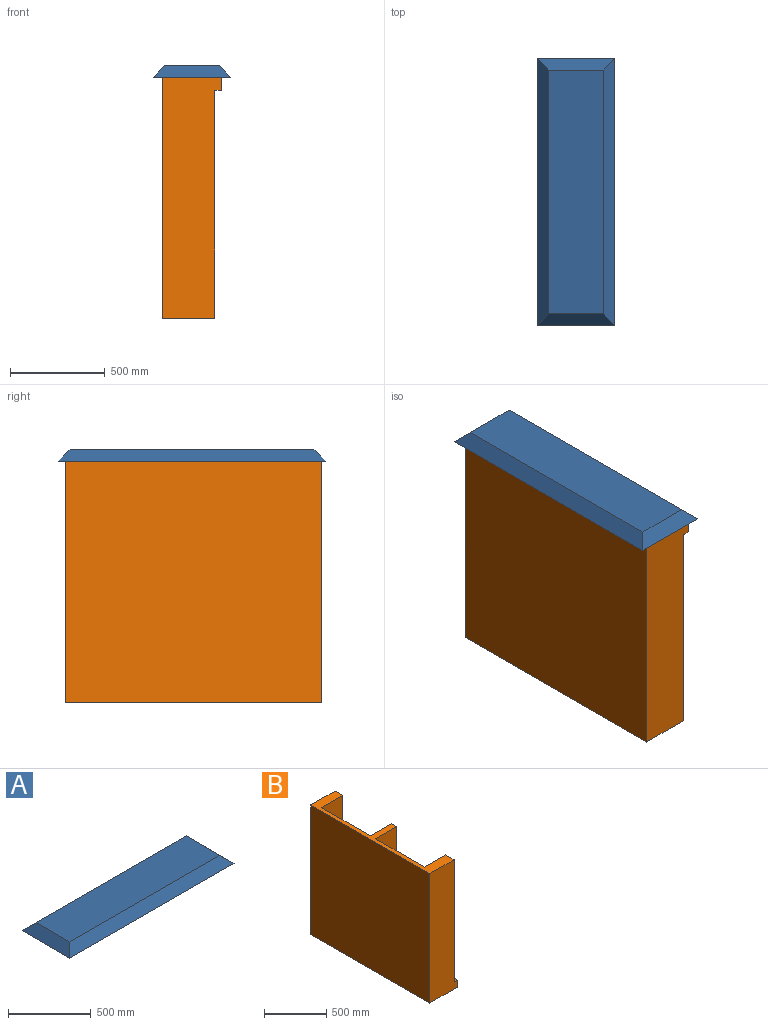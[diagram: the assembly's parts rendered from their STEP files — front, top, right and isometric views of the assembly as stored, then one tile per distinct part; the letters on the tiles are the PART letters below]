
ASSEMBLY  parts=2 mates=1
PART A: 6 faces, bbox 1405x410x60 mm
  f0: plane 1285x290mm, normal (0,0,1), area 372650mm2, adj f2,f3,f4,f5
  f1: plane 1405x410mm, normal (0,0,-1), area 576050mm2, adj f2,f3,f4,f5
  f2: plane 1405x60mm, normal (0,0.71,0.71), area 114127mm2, adj f0,f1,f3,f4
  f3: plane 410x60mm, normal (0.71,0,0.71), area 29698.5mm2, adj f0,f1,f2,f5
  f4: plane 410x60mm, normal (-0.71,0,0.71), area 29698.5mm2, adj f0,f1,f2,f5
  f5: plane 1405x60mm, normal (0,-0.71,0.71), area 114127mm2, adj f0,f1,f3,f4
PART B: 34 faces, bbox 310x1350x1270 mm
  f0: plane 345x240mm, normal (0,1,0), area 82800mm2, adj f2,f23,f28,f33
  f1: plane 285x240mm, normal (0,1,0), area 68400mm2, adj f13,f23,f26,f32
  f2: plane 554.25x345mm, normal (1,0,0), area 191217.5mm2, adj f0,f10,f28,f33
  f3: plane 553x345mm, normal (1,0,0), area 190785mm2, adj f4,f11,f27,f30
  f4: plane 345x240mm, normal (0,-1,0), area 82800mm2, adj f3,f23,f27,f30
  f5: plane 285x240mm, normal (0,-1,0), area 68400mm2, adj f13,f23,f26,f32
  f6: plane 285x240mm, normal (0,1,0), area 68400mm2, adj f16,f23,f26,f31
  f7: plane 240x70mm, normal (0,1,0), area 16800mm2, adj f8,f12,f15,f21
  f8: plane 1167.25x520mm, normal (1,0,0), area 602771.9mm2, adj f7,f9,f12,f21,f24,f25,f29
  f9: plane 520x240mm, normal (0,-1,0), area 124800mm2, adj f8,f15,f21,f23,f29
  f10: plane 345x240mm, normal (0,-1,0), area 82800mm2, adj f2,f23,f28,f33
  f11: plane 345x240mm, normal (0,1,0), area 82800mm2, adj f3,f23,f27,f30
  f12: plane 1350x275mm, normal (0,0,1), area 61650mm2, adj f7,f8,f14,f15,f18,f19,f20,f23
  f13: plane 554.25x285mm, normal (1,0,0), area 157962.3mm2, adj f1,f5,f26,f32
  f14: plane 554.25x70mm, normal (-1,0,0), area 38797.8mm2, adj f12,f21,f24,f25
  f15: plane 553x70mm, normal (-1,0,0), area 38710mm2, adj f7,f9,f12,f21
  f16: plane 553x285mm, normal (1,0,0), area 157605mm2, adj f6,f22,f26,f31
  f17: plane 1350x1270mm, normal (-1,0,0), area 1714500mm2, adj f18,f20,f21,f26
  f18: plane 1270x310mm, normal (0,-1,0), area 351700mm2, adj f12,f17,f19,f21,f23,f26
  f19: plane 1350x70mm, normal (1,0,0), area 94500mm2, adj f12,f18,f20,f21
  f20: plane 1270x310mm, normal (0,1,0), area 351700mm2, adj f12,f17,f19,f21,f23,f26
  f21: plane 1350x310mm, normal (0,0,-1), area 152759.1mm2, adj f7,f8,f9,f14,f15,f17,f18,f19
  f22: plane 285x240mm, normal (0,-1,0), area 68400mm2, adj f16,f23,f26,f31
  f23: plane 1350x1200mm, normal (1,0,0), area 397166.1mm2, adj f0,f1,f4,f5,f6,f9,f10,f11
  f24: plane 520x240mm, normal (0,1,0), area 124800mm2, adj f8,f14,f21,f23,f29
  f25: plane 240x70mm, normal (0,-1,0), area 16800mm2, adj f8,f12,f14,f21
  f26: plane 1350x275mm, normal (0,0,1), area 105509.1mm2, adj f1,f5,f6,f13,f16,f17,f18,f20
  f27: plane 553x240mm, normal (0,0,1), area 132720mm2, adj f3,f4,f11,f23
  f28: plane 554.25x240mm, normal (0,0,1), area 133020.9mm2, adj f0,f2,f10,f23
  f29: plane 1167.25x240mm, normal (0,0,-1), area 280140.9mm2, adj f8,f9,f23,f24
  f30: plane 553x240mm, normal (0,0,-1), area 132720mm2, adj f3,f4,f11,f23
  f31: plane 553x240mm, normal (0,0,1), area 132720mm2, adj f6,f16,f22,f23
  f32: plane 554.25x240mm, normal (0,0,1), area 133020.9mm2, adj f1,f5,f13,f23
  f33: plane 554.25x240mm, normal (0,0,-1), area 133020.9mm2, adj f0,f2,f10,f23
PLACE A rot(axis=(0,0,1),90deg) t=(-801.07,-868.68,1367.42)mm
PLACE B rot(axis=(1,0,0),180deg) t=(-490.82,184.58,1367.42)mm
MATE fastened A.f1 <-> B.f21  axis (0,0,-1) through (-983.77,-237.22,1367.42)mm
